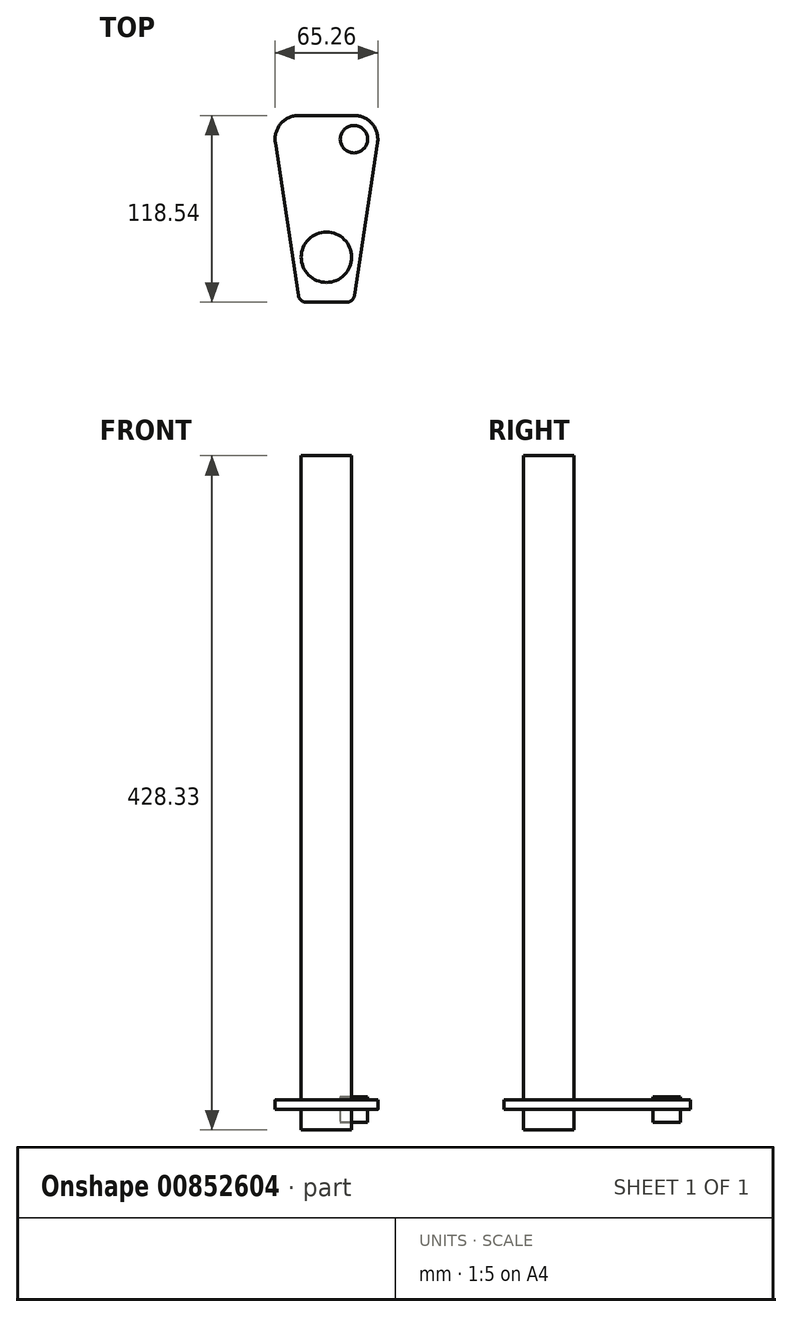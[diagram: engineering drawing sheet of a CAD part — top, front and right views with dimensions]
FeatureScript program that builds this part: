
annotation { "Feature Type Name" : "Feature", "Feature Type Description" : "" }
export const myFeature = defineFeature(function(context is Context, id is Id, definition is map)
    precondition{}
    {
        {
            var Q0;
            Q0=qCreatedBy(makeId("Top.planeOp"),FACE);
            var sketch = newSketch(context, id + "F0", { "sketchPlane" : qUnion([Q0])});
            skCircle(sketch, "E0", {"center": v(0, 0) * mm, "radius": 16 * mm});
            skCircle(sketch, "E1", {"center": v(17.5, 75) * mm, "radius": 8.75 * mm});
            skCircle(sketch, "E2.MirrorC", {"center": v(-17.5, 75) * mm, "radius": 8.75 * mm});
            skSolve(sketch);
        }
        {
            var Q0;
            Q0=qCreatedBy(makeId("Top.planeOp"),FACE);
            var sketch = newSketch(context, id + "F1", { "sketchPlane" : qUnion([Q0])});
            skLineSegment(sketch, "E3", {"start": v(0, -28.53) * mm, "end": v(12.89, -28.53) * mm});
            skLineSegment(sketch, "E4", {"start": v(17.83, -24.27) * mm, "end": v(32.47, 72.78) * mm});
            skLineSegment(sketch, "E5", {"start": v(17.63, 90.01) * mm, "end": v(0, 90.01) * mm});
            skPoint(sketch, "E6.visualSharp", {"position": v(35.06, 90.01) * mm});
            skArc(sketch, "E6.filletArc", {"start": v(32.47, 72.78) * mm, "mid": v(29, 84.8) * mm, "end": v(17.63, 90.01) * mm});
            skPoint(sketch, "E7.visualSharp", {"position": v(17.2, -28.53) * mm});
            skArc(sketch, "E7.filletArc", {"start": v(12.89, -28.53) * mm, "mid": v(16.15, -27.32) * mm, "end": v(17.83, -24.27) * mm});
            skLineSegment(sketch, "E8.MirrorCS", {"start": v(-17.63, 90.01) * mm, "end": v(0, 90.01) * mm});
            skArc(sketch, "E9.MirrorCS", {"start": v(-32.47, 72.78) * mm, "mid": v(-29, 84.8) * mm, "end": v(-17.63, 90.01) * mm});
            skLineSegment(sketch, "E10.MirrorCS", {"start": v(-17.83, -24.27) * mm, "end": v(-32.47, 72.78) * mm});
            skLineSegment(sketch, "E11.MirrorCS", {"start": v(0, -28.53) * mm, "end": v(-12.89, -28.53) * mm});
            skArc(sketch, "E12.MirrorCS", {"start": v(-12.89, -28.53) * mm, "mid": v(-16.15, -27.32) * mm, "end": v(-17.83, -24.27) * mm});
            skSolve(sketch);
        }
        {
            var Q0;
            Q0=makeQuery(id+"F1.imprint","IMPRINT",FACE,{"disambiguationData":[TD([[makeQuery(id+"F1.imprint","IMPRINT",EDGE,{"derivedFrom":sQuery(id+"F1.wireOp",EDGE,"E3")}),1.0]])]});
            extrude(context, id + "F2", {"entities" : qUnion([Q0]), "depth" : 6 * mm, "offsetDistance" : 25 * mm});
        }
        {
            var Q0;
            Q0=makeQuery(id+"F0.imprint","IMPRINT",FACE,{"disambiguationData":[TD([[makeQuery(id+"F0.imprint","IMPRINT",EDGE,{"derivedFrom":sQuery(id+"F0.wireOp",EDGE,"E0")}),1.0]])]});
            extrude(context, id + "F3", {"entities" : qUnion([Q0]), "operationType" : NewBodyOperationType.ADD, "depth" : 415.33 * mm, "offsetDistance" : 25 * mm});
        }
        {
            var Q0;
            Q0=makeQuery(id+"F0.imprint","IMPRINT",FACE,{"disambiguationData":[TD([[makeQuery(id+"F0.imprint","IMPRINT",EDGE,{"derivedFrom":sQuery(id+"F0.wireOp",EDGE,"E1")}),1.0]])]});
            var Q1;
            Q1=makeQuery(id+"F0.imprint","IMPRINT",FACE,{"disambiguationData":[TD([[makeQuery(id+"F0.imprint","IMPRINT",EDGE,{"derivedFrom":sQuery(id+"F0.wireOp",EDGE,"E2.MirrorC")}),-1.0]])]});
            extrude(context, id + "F4", {"entities" : qUnion([Q0, Q1]), "operationType" : NewBodyOperationType.ADD, "depth" : 16 * mm, "offsetDistance" : 25 * mm, "symmetric" : true});
        }
        {
            var Q0;
            Q0=makeQuery(id+"F0.imprint","IMPRINT",FACE,{"disambiguationData":[TD([[makeQuery(id+"F0.imprint","IMPRINT",EDGE,{"derivedFrom":sQuery(id+"F0.wireOp",EDGE,"E0")}),1.0]])]});
            extrude(context, id + "F5", {"entities" : qUnion([Q0]), "operationType" : NewBodyOperationType.ADD, "oppositeDirection" : true, "depth" : 13 * mm, "offsetDistance" : 25 * mm});
        }
    });
